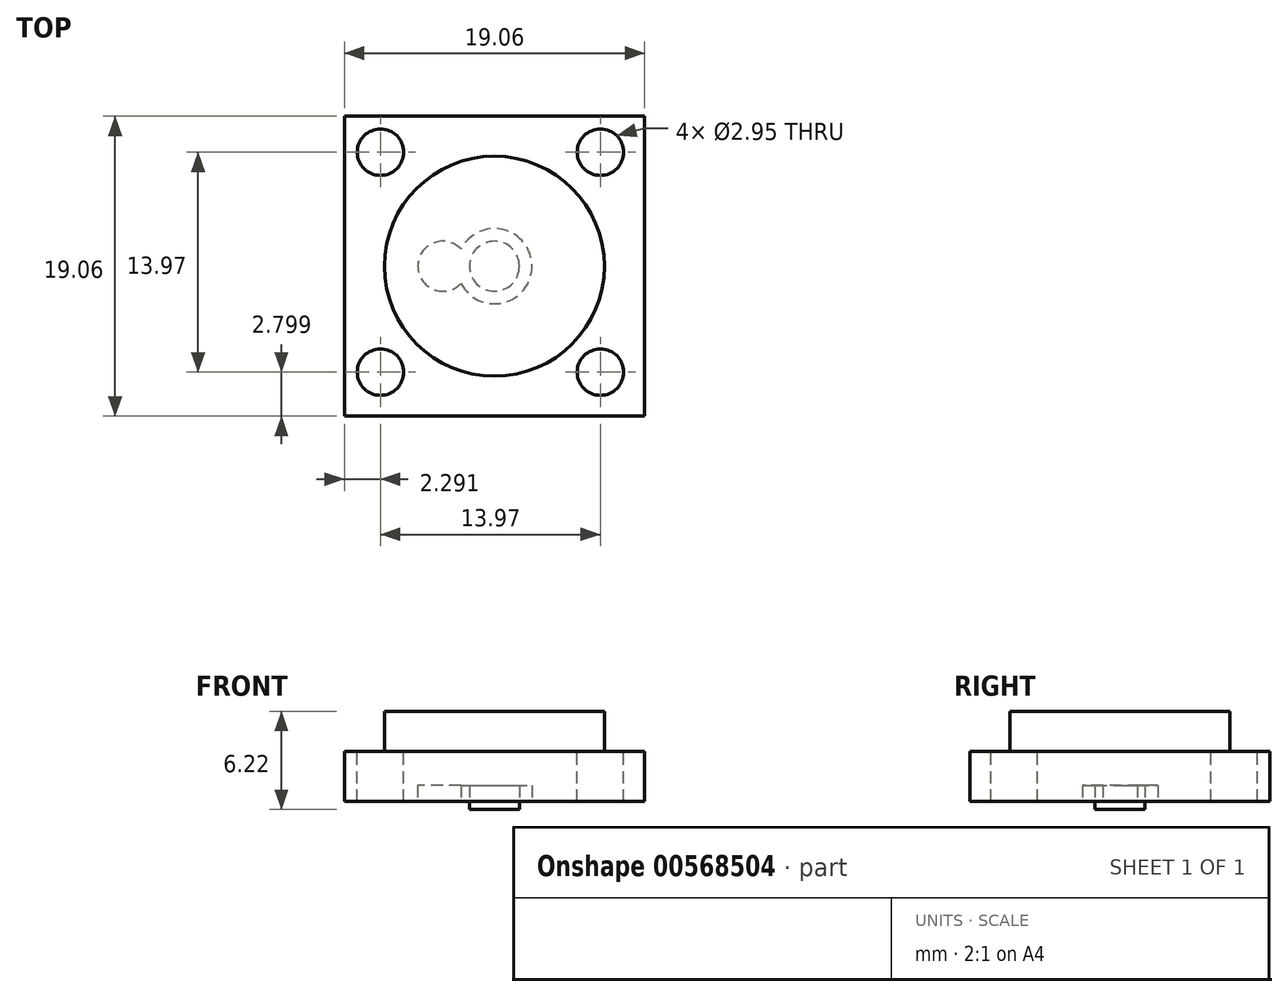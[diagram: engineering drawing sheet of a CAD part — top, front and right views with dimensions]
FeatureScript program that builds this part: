
annotation { "Feature Type Name" : "Feature", "Feature Type Description" : "" }
export const myFeature = defineFeature(function(context is Context, id is Id, definition is map)
    precondition{}
    {
        {
            var Q0;
            Q0=qCreatedBy(makeId("Top.planeOp"),FACE);
            var sketch = newSketch(context, id + "F0", { "sketchPlane" : qUnion([Q0])});
            skLineSegment(sketch, "E0.bottom", {"start": v(-9.53, 9.53) * mm, "end": v(9.53, 9.53) * mm});
            skLineSegment(sketch, "E0.top", {"start": v(-9.53, -9.53) * mm, "end": v(9.53, -9.53) * mm});
            skLineSegment(sketch, "E0.left", {"start": v(-9.52, 9.53) * mm, "end": v(-9.53, -9.53) * mm});
            skLineSegment(sketch, "E0.right", {"start": v(9.53, 9.53) * mm, "end": v(9.53, -9.53) * mm});
            skPoint(sketch, "E0.middle", {"position": v(0, 0) * mm});
            skSolve(sketch);
        }
        {
            var Q0;
            Q0 = qSketchRegion(id + "F0", true);
            extrude(context, id + "F1", {"entities" : qUnion([Q0]), "depth" : 6.22 * mm, "offsetDistance" : 25.4 * mm});
        }
        {
            var Q0;
            Q0=makeQuery(id+"F1.opExtrude","CAP_FACE",FACE,{"disambiguationData":[OSD([sQuery(id+"F0.wireOp",EDGE,"E0.bottom"),sQuery(id+"F0.wireOp",EDGE,"E0.top"),sQuery(id+"F0.wireOp",EDGE,"E0.left"),sQuery(id+"F0.wireOp",EDGE,"E0.right")])],"isStart":false});
            var sketch = newSketch(context, id + "F2", { "sketchPlane" : qUnion([Q0])});
            skCircle(sketch, "E1", {"center": v(0, 0) * mm, "radius": 6.99 * mm});
            skLineSegment(sketch, "E2.bottom", {"start": v(-9.53, 9.53) * mm, "end": v(9.53, 9.53) * mm});
            skLineSegment(sketch, "E2.top", {"start": v(-9.53, -9.53) * mm, "end": v(9.53, -9.53) * mm});
            skLineSegment(sketch, "E2.left", {"start": v(-9.53, 9.53) * mm, "end": v(-9.53, -9.53) * mm});
            skLineSegment(sketch, "E2.right", {"start": v(9.53, 9.53) * mm, "end": v(9.53, -9.53) * mm});
            skSolve(sketch);
        }
        {
            var Q0;
            Q0 = qSketchRegion(id + "F2", true);
            extrude(context, id + "F3", {"entities" : qUnion([Q0]), "operationType" : NewBodyOperationType.REMOVE, "oppositeDirection" : true, "depth" : 2.54 * mm, "offsetDistance" : 25.4 * mm});
        }
        {
            var Q0;
            Q0=makeQuery(id+"F3.boolean.opBoolean","COPY",FACE,{"derivedFrom":makeQuery(id+"F3.opExtrude","CAP_FACE",FACE,{"disambiguationData":[OSD([sQuery(id+"F2.wireOp",EDGE,"E1"),sQuery(id+"F2.wireOp",EDGE,"E2.bottom"),sQuery(id+"F2.wireOp",EDGE,"E2.top"),sQuery(id+"F2.wireOp",EDGE,"E2.left"),sQuery(id+"F2.wireOp",EDGE,"E2.right")])],"isStart":false})});
            var sketch = newSketch(context, id + "F4", { "sketchPlane" : qUnion([Q0])});
            skCircle(sketch, "E3", {"center": v(-7.24, 7.24) * mm, "radius": 1.47 * mm});
            skCircle(sketch, "E4.0.1.0", {"center": v(-7.24, -6.73) * mm, "radius": 1.47 * mm});
            skCircle(sketch, "E4.1.0.0", {"center": v(6.73, 7.24) * mm, "radius": 1.47 * mm});
            skCircle(sketch, "E4.1.1.0", {"center": v(6.73, -6.73) * mm, "radius": 1.47 * mm});
            skLineSegment(sketch, "E4.direction1", {"start": v(-7.24, 7.24) * mm, "end": v(6.73, 7.24) * mm, "construction": true});
            skLineSegment(sketch, "E4.direction2", {"start": v(-7.24, 7.24) * mm, "end": v(-7.24, -6.73) * mm, "construction": true});
            skSolve(sketch);
        }
        {
            var Q0;
            Q0 = qSketchRegion(id + "F4", true);
            extrude(context, id + "F5", {"entities" : qUnion([Q0]), "operationType" : NewBodyOperationType.REMOVE, "endBound" : BoundingType.THROUGH_ALL, "oppositeDirection" : true, "depth" : 25.4 * mm, "offsetDistance" : 25.4 * mm});
        }
        {
            var Q0;
            Q0=makeQuery(id+"F1.opExtrude","CAP_FACE",FACE,{"disambiguationData":[OSD([sQuery(id+"F0.wireOp",EDGE,"E0.bottom"),sQuery(id+"F0.wireOp",EDGE,"E0.top"),sQuery(id+"F0.wireOp",EDGE,"E0.left"),sQuery(id+"F0.wireOp",EDGE,"E0.right")])],"isStart":true});
            var sketch = newSketch(context, id + "F6", { "sketchPlane" : qUnion([Q0])});
            skCircle(sketch, "E5", {"center": v(0, 0) * mm, "radius": 1.59 * mm});
            skLineSegment(sketch, "E6.bottom", {"start": v(-9.53, 9.53) * mm, "end": v(9.53, 9.53) * mm});
            skLineSegment(sketch, "E6.top", {"start": v(-9.53, -9.53) * mm, "end": v(9.53, -9.53) * mm});
            skLineSegment(sketch, "E6.left", {"start": v(-9.53, 9.53) * mm, "end": v(-9.53, -9.53) * mm});
            skLineSegment(sketch, "E6.right", {"start": v(9.53, 9.53) * mm, "end": v(9.53, -9.53) * mm});
            skSolve(sketch);
        }
        {
            var Q0;
            Q0 = qSketchRegion(id + "F6", true);
            extrude(context, id + "F7", {"entities" : qUnion([Q0]), "operationType" : NewBodyOperationType.REMOVE, "oppositeDirection" : true, "depth" : 0.5 * mm, "offsetDistance" : 25.4 * mm});
        }
        {
            var Q0;
            Q0=makeQuery(id+"F7.boolean.opBoolean","COPY",FACE,{"derivedFrom":makeQuery(id+"F7.opExtrude","CAP_FACE",FACE,{"disambiguationData":[OSD([sQuery(id+"F6.wireOp",EDGE,"E5"),sQuery(id+"F6.wireOp",EDGE,"E6.bottom"),sQuery(id+"F6.wireOp",EDGE,"E6.top"),sQuery(id+"F6.wireOp",EDGE,"E6.left"),sQuery(id+"F6.wireOp",EDGE,"E6.right")])],"isStart":false})});
            var sketch = newSketch(context, id + "F8", { "sketchPlane" : qUnion([Q0])});
            skCircle(sketch, "E7", {"center": v(-3.28, 0) * mm, "radius": 1.59 * mm});
            skCircle(sketch, "E8", {"center": v(0, 0) * mm, "radius": 2.39 * mm});
            skCircle(sketch, "E9", {"center": v(0, 0) * mm, "radius": 1.59 * mm});
            skSolve(sketch);
        }
        {
            var Q0;
            Q0 = qSketchRegion(id + "F8", true);
            extrude(context, id + "F9", {"entities" : qUnion([Q0]), "operationType" : NewBodyOperationType.REMOVE, "oppositeDirection" : true, "depth" : 1.02 * mm, "offsetDistance" : 25.4 * mm});
        }
    });
